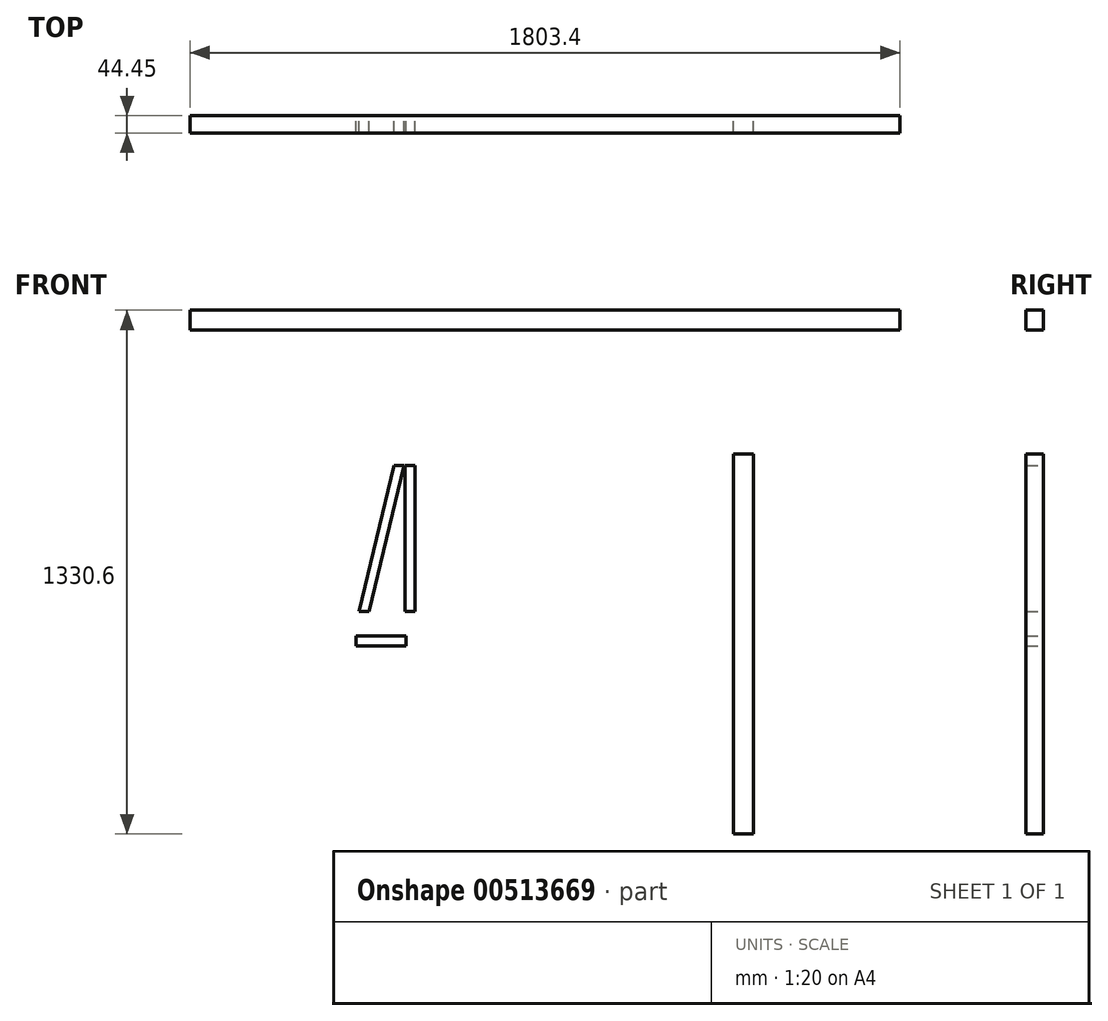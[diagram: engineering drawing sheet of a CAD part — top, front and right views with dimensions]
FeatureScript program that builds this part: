
annotation { "Feature Type Name" : "Feature", "Feature Type Description" : "" }
export const myFeature = defineFeature(function(context is Context, id is Id, definition is map)
    precondition{}
    {
        {
            var Q0;
            Q0=qCreatedBy(makeId("Front.planeOp"),FACE);
            var sketch = newSketch(context, id + "F0", { "sketchPlane" : qUnion([Q0])});
            skLineSegment(sketch, "E0", {"start": v(228.45, 0) * mm, "end": v(253.85, 0) * mm});
            skLineSegment(sketch, "E1", {"start": v(253.85, 0) * mm, "end": v(342.16, 370.62) * mm});
            skLineSegment(sketch, "E2", {"start": v(342.16, 370.62) * mm, "end": v(316.76, 370.62) * mm});
            skLineSegment(sketch, "E3", {"start": v(316.76, 370.62) * mm, "end": v(228.45, 0) * mm});
            skLineSegment(sketch, "E4", {"start": v(220.26, -61.84) * mm, "end": v(347.26, -61.84) * mm});
            skLineSegment(sketch, "E5", {"start": v(347.26, -61.84) * mm, "end": v(347.26, -87.24) * mm});
            skLineSegment(sketch, "E6", {"start": v(347.26, -87.24) * mm, "end": v(220.26, -87.24) * mm});
            skLineSegment(sketch, "E7", {"start": v(220.26, -87.24) * mm, "end": v(220.26, -61.84) * mm});
            skLineSegment(sketch, "E8", {"start": v(-200.86, 765.52) * mm, "end": v(1602.54, 765.52) * mm});
            skLineSegment(sketch, "E9", {"start": v(1602.54, 765.52) * mm, "end": v(1602.54, 714.72) * mm});
            skLineSegment(sketch, "E10", {"start": v(1602.54, 714.72) * mm, "end": v(-200.86, 714.72) * mm});
            skLineSegment(sketch, "E11", {"start": v(-200.86, 714.72) * mm, "end": v(-200.86, 765.52) * mm});
            skLineSegment(sketch, "E12", {"start": v(1179.08, 400.12) * mm, "end": v(1229.88, 400.12) * mm});
            skLineSegment(sketch, "E13", {"start": v(1229.88, 400.12) * mm, "end": v(1229.88, -565.08) * mm});
            skLineSegment(sketch, "E14", {"start": v(1229.88, -565.08) * mm, "end": v(1179.08, -565.08) * mm});
            skLineSegment(sketch, "E15", {"start": v(1179.08, -565.08) * mm, "end": v(1179.08, 400.12) * mm});
            skLineSegment(sketch, "E16", {"start": v(345.14, 0) * mm, "end": v(370.54, 0) * mm});
            skLineSegment(sketch, "E17", {"start": v(370.54, 0) * mm, "end": v(370.54, 370.62) * mm});
            skLineSegment(sketch, "E18", {"start": v(370.54, 370.62) * mm, "end": v(345.14, 370.62) * mm});
            skLineSegment(sketch, "E19", {"start": v(345.14, 370.62) * mm, "end": v(345.14, 0) * mm});
            skSolve(sketch);
        }
        {
            var Q0;
            Q0=makeQuery(id+"F0.imprint","IMPRINT",FACE,{"disambiguationData":[TD([[makeQuery(id+"F0.imprint","IMPRINT",EDGE,{"derivedFrom":sQuery(id+"F0.wireOp",EDGE,"E0")}),1.0]])]});
            var Q1;
            Q1=makeQuery(id+"F0.imprint","IMPRINT",FACE,{"disambiguationData":[TD([[makeQuery(id+"F0.imprint","IMPRINT",EDGE,{"derivedFrom":sQuery(id+"F0.wireOp",EDGE,"E4")}),-1.0]])]});
            var Q2;
            Q2=makeQuery(id+"F0.imprint","IMPRINT",FACE,{"disambiguationData":[TD([[makeQuery(id+"F0.imprint","IMPRINT",EDGE,{"derivedFrom":sQuery(id+"F0.wireOp",EDGE,"yXmKyTsn-JguS-DGiU-dm3Q-G86C9TfDAE1V")}),-1.0]])]});
            var Q3;
            Q3=makeQuery(id+"F0.imprint","IMPRINT",FACE,{"disambiguationData":[TD([[makeQuery(id+"F0.imprint","IMPRINT",EDGE,{"derivedFrom":sQuery(id+"F0.wireOp",EDGE,"E12")}),-1.0]])]});
            var Q4;
            Q4=makeQuery(id+"F0.imprint","IMPRINT",FACE,{"disambiguationData":[TD([[makeQuery(id+"F0.imprint","IMPRINT",EDGE,{"derivedFrom":sQuery(id+"F0.wireOp",EDGE,"E8")}),-1.0]])]});
            var Q5;
            Q5=makeQuery(id+"F0.imprint","IMPRINT",FACE,{"disambiguationData":[TD([[makeQuery(id+"F0.imprint","IMPRINT",EDGE,{"derivedFrom":sQuery(id+"F0.wireOp",EDGE,"E16")}),1.0]])]});
            extrude(context, id + "F1", {"entities" : qUnion([Q0, Q1, Q2, Q3, Q4, Q5]), "depth" : 44.45 * mm});
        }
    });
